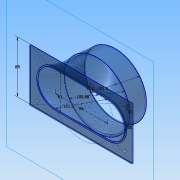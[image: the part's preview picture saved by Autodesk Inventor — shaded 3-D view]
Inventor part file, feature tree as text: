
AUTODESK INVENTOR PART (.ipt)
format: ipt  version: 2014 SP2 (Build 180246200, 246)  size: 389,120 bytes
history: native  units: mm
features: sketch x3, plane x2, loft x2, mirror x2, shell x1, fillet x1, extrude x1, hole x1
ambient origin geometry x8: Origin, YZ Plane, XZ Plane, XY Plane, X Axis, Y Axis, Z Axis, Center Point
bodies: Solid1 (feature_tree)
feature tree (13):
  sketch  "Sketch1"  dims[d0=101.6mm d1=85.0mm]
  plane  "Work Plane1"
  plane  "Work Plane2"
  sketch  "Sketch2"  dims[d2=61.0mm d3=10.0mm d4=12.0mm d5=12.0mm]
  sketch  "Sketch3"  dims[d6=25.0mm d7=106.68mm d10=0.0mm d11=90.0deg d12=30.0mm d13=101.6mm d22=0.0mm d23=90.0deg d30=0.0mm d31=90.0deg d32=0.0mm d33=90.0deg d35=2.0mm d36=2.0mm d37=0.0mm d38=2.0mm d43=4.4mm d44=6.0mm d45=4.0mm d46=2.0mm d47=90.0deg d48=8.0mm d49=20.594885mm d50=86.0mm]
  loft  "Loft1"
  loft  "Loft2"
  shell  "Shell1"  Thickness=12.0mm
  fillet  "Fillet1"  Radius=12.0mm
  extrude  "Extrusion1"  Depth=2.0mm
  hole  "Hole1"  [1 undecoded]
  mirror  "Mirror1"
  mirror  "Mirror2"
note: 1 required parameter value undecoded (feature->parameter linkage not recoverable at this tier; creation-order binding heuristic only, values carry confidence <= 0.55)
